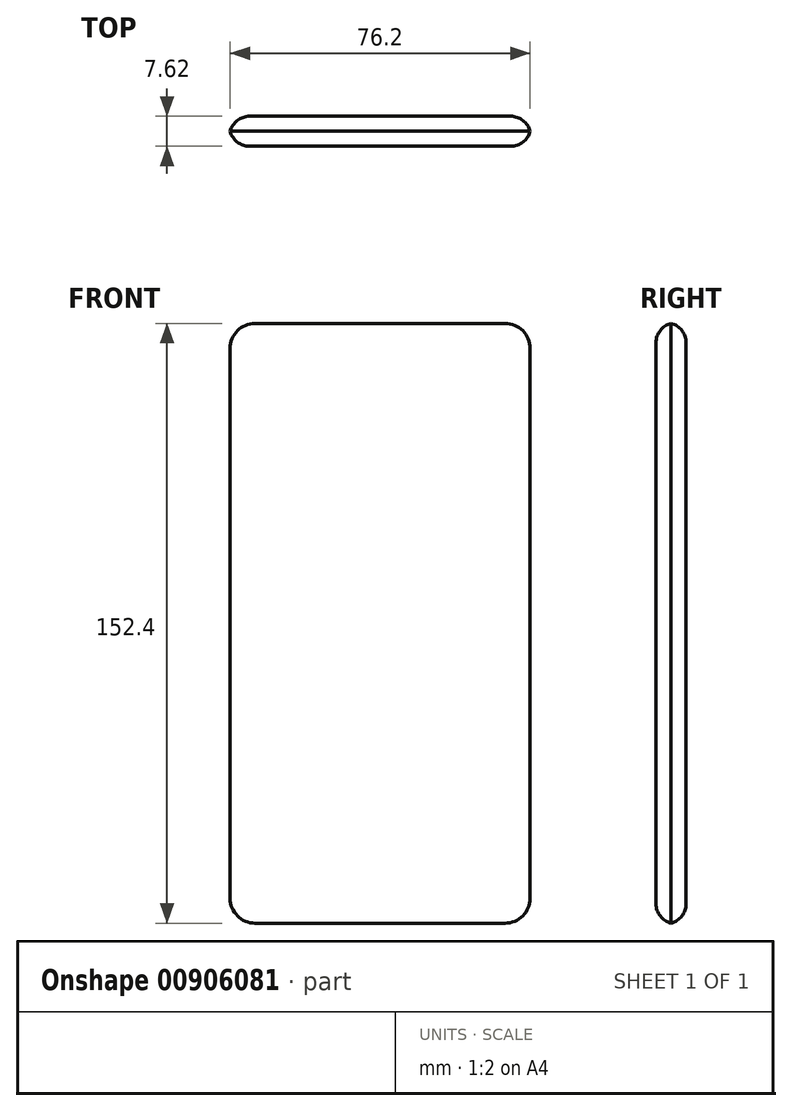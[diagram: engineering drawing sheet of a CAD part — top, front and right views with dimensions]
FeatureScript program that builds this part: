
annotation { "Feature Type Name" : "Feature", "Feature Type Description" : "" }
export const myFeature = defineFeature(function(context is Context, id is Id, definition is map)
    precondition{}
    {
        {
            var Q0;
            Q0=qCreatedBy(makeId("Front.planeOp"),FACE);
            var sketch = newSketch(context, id + "F0", { "sketchPlane" : qUnion([Q0])});
            skLineSegment(sketch, "E0.bottom", {"start": v(31.75, -76.2) * mm, "end": v(-31.75, -76.2) * mm});
            skLineSegment(sketch, "E0.top", {"start": v(31.75, 76.2) * mm, "end": v(-31.75, 76.2) * mm});
            skLineSegment(sketch, "E0.left", {"start": v(38.1, -69.85) * mm, "end": v(38.1, 69.85) * mm});
            skLineSegment(sketch, "E0.right", {"start": v(-38.1, -69.85) * mm, "end": v(-38.1, 69.85) * mm});
            skPoint(sketch, "E0.middle", {"position": v(0, 0) * mm});
            skPoint(sketch, "E1.visualSharp", {"position": v(-38.1, 76.2) * mm});
            skArc(sketch, "E1.filletArc", {"start": v(-31.75, 76.2) * mm, "mid": v(-36.24, 74.34) * mm, "end": v(-38.1, 69.85) * mm});
            skPoint(sketch, "E2.visualSharp", {"position": v(38.1, 76.2) * mm});
            skArc(sketch, "E2.filletArc", {"start": v(38.1, 69.85) * mm, "mid": v(36.24, 74.34) * mm, "end": v(31.75, 76.2) * mm});
            skPoint(sketch, "E3.visualSharp", {"position": v(-38.1, -76.2) * mm});
            skArc(sketch, "E3.filletArc", {"start": v(-38.1, -69.85) * mm, "mid": v(-36.24, -74.34) * mm, "end": v(-31.75, -76.2) * mm});
            skPoint(sketch, "E4.visualSharp", {"position": v(38.1, -76.2) * mm});
            skArc(sketch, "E4.filletArc", {"start": v(31.75, -76.2) * mm, "mid": v(36.24, -74.34) * mm, "end": v(38.1, -69.85) * mm});
            skSolve(sketch);
        }
        {
            var Q0;
            Q0 = qSketchRegion(id + "F0", true);
            extrude(context, id + "F1", {"entities" : qUnion([Q0]), "depth" : 3.8 * mm, "offsetDistance" : 25.4 * mm});
        }
        {
            var Q0;
            Q0=makeQuery(id+"F1.opExtrude","CAP_EDGE",EDGE,{"disambiguationData":[OSD([sQuery(id+"F0.wireOp",EDGE,"E0.left")])],"isStart":false});
            fillet(context, id + "F2", {"entities" : qUnion([Q0]), "radius" : 5.08 * mm, "tangentPropagation" : true, "allowEdgeOverflow" : false});
        }
        {
            var Q0;
            Q0=makeQuery(id+"F1.opExtrude","CAP_FACE",FACE,{"disambiguationData":[OSD([sQuery(id+"F0.wireOp",EDGE,"E0.bottom"),sQuery(id+"F0.wireOp",EDGE,"E0.top"),sQuery(id+"F0.wireOp",EDGE,"E0.left"),sQuery(id+"F0.wireOp",EDGE,"E0.right"),sQuery(id+"F0.wireOp",EDGE,"E1.filletArc"),sQuery(id+"F0.wireOp",EDGE,"E2.filletArc"),sQuery(id+"F0.wireOp",EDGE,"E3.filletArc"),sQuery(id+"F0.wireOp",EDGE,"E4.filletArc")])],"isStart":true});
            extrude(context, id + "F3", {"entities" : qUnion([Q0]), "operationType" : NewBodyOperationType.ADD, "depth" : 3.8 * mm, "offsetDistance" : 25.4 * mm});
        }
        {
            var Q0;
            Q0=makeQuery(id+"F3.opExtrude","CAP_EDGE",EDGE,{"disambiguationData":[OSD([sQuery(id+"F0.wireOp",EDGE,"E0.left")])],"isStart":false});
            fillet(context, id + "F4", {"entities" : qUnion([Q0]), "radius" : 5.08 * mm, "tangentPropagation" : true, "allowEdgeOverflow" : false});
        }
        {
            var Q0;
            Q0=qCreatedBy(makeId("Front.planeOp"),FACE);
            var sketch = newSketch(context, id + "F5", { "sketchPlane" : qUnion([Q0])});
            skCircle(sketch, "E5", {"center": v(-22.85, 60.49) * mm, "radius": 6.35 * mm});
            skSolve(sketch);
        }
        {
            var Q0;
            Q0=sQuery(id+"F5.wireOp",EDGE,"E5");
            extrude(context, id + "F6", {"bodyType" : ToolBodyType.SURFACE, "surfaceEntities" : qUnion([Q0]), "oppositeDirection" : true, "depth" : 1.27 * mm, "offsetDistance" : 25.4 * mm});
        }
    });
